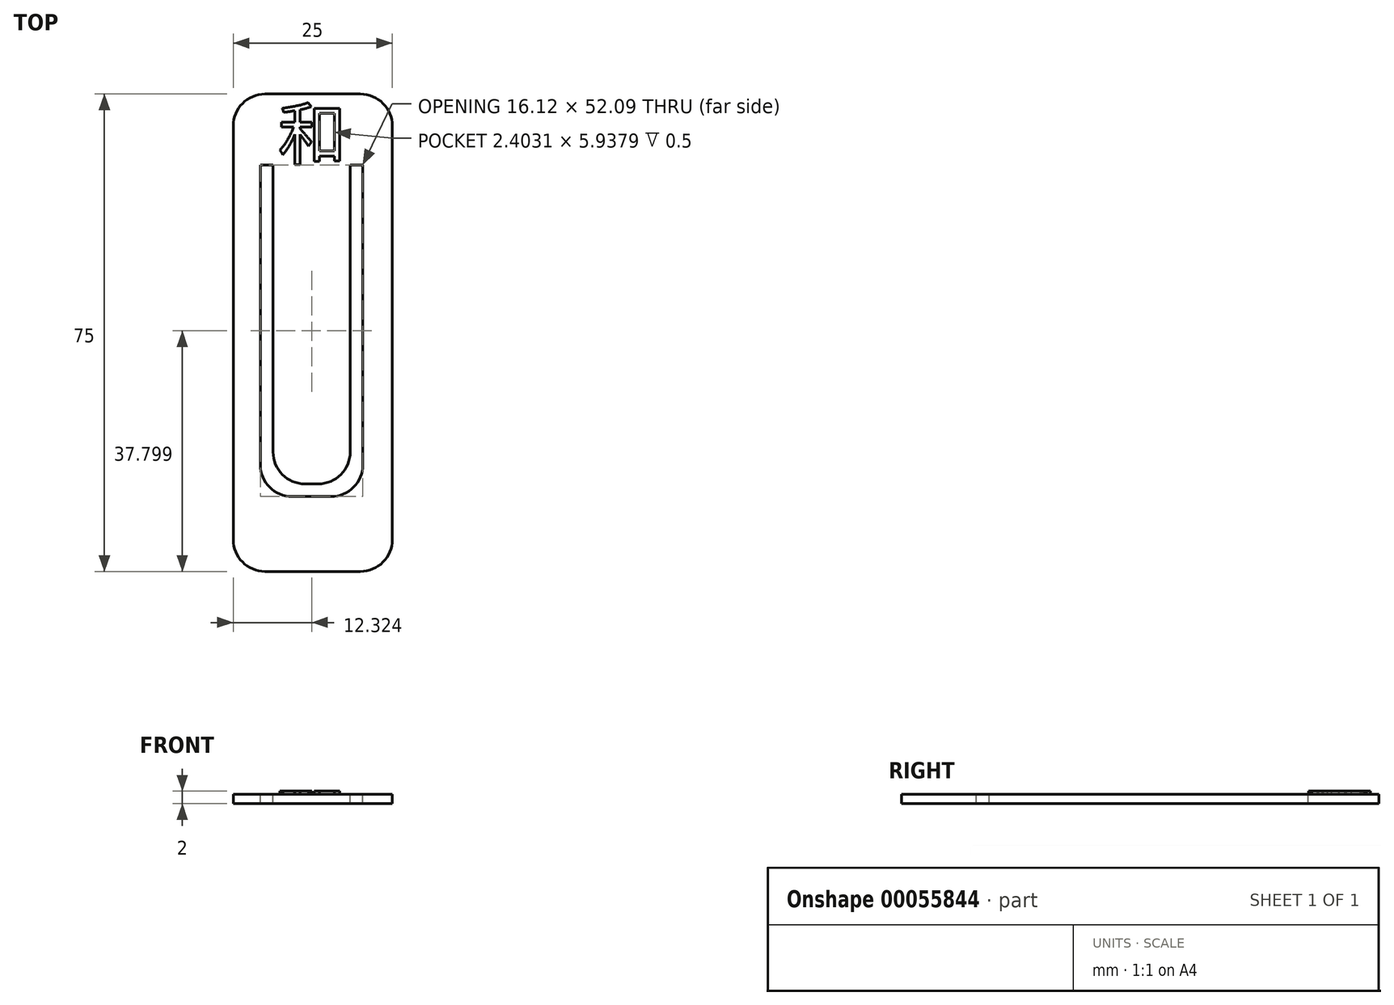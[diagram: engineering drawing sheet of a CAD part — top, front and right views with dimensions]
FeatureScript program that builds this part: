
annotation { "Feature Type Name" : "Feature", "Feature Type Description" : "" }
export const myFeature = defineFeature(function(context is Context, id is Id, definition is map)
    precondition{}
    {
        {
            var Q0;
            Q0=qCreatedBy(makeId("Top.planeOp"),FACE);
            var sketch = newSketch(context, id + "F0", { "sketchPlane" : qUnion([Q0])});
            skLineSegment(sketch, "E0.bottom", {"start": v(-9.97, 72.6) * mm, "end": v(15.03, 72.6) * mm});
            skLineSegment(sketch, "E0.top", {"start": v(-9.97, -2.4) * mm, "end": v(15.03, -2.4) * mm});
            skLineSegment(sketch, "E0.left", {"start": v(-9.97, 72.6) * mm, "end": v(-9.97, -2.4) * mm});
            skLineSegment(sketch, "E0.right", {"start": v(15.03, 72.6) * mm, "end": v(15.03, -2.4) * mm});
            skSolve(sketch);
        }
        {
            var Q0;
            Q0=makeQuery(id+"F0.imprint","IMPRINT",FACE,{"disambiguationData":[TD([[makeQuery(id+"F0.imprint","IMPRINT",EDGE,{"derivedFrom":sQuery(id+"F0.wireOp",EDGE,"E0.bottom")}),-1.0]])]});
            extrude(context, id + "F1", {"entities" : qUnion([Q0]), "depth" : 1.5 * mm});
        }
        {
            var Q0;
            Q0=makeQuery(id+"F1.opExtrude","CAP_FACE",FACE,{"disambiguationData":[OSD([sQuery(id+"F0.wireOp",EDGE,"E0.bottom"),sQuery(id+"F0.wireOp",EDGE,"E0.top"),sQuery(id+"F0.wireOp",EDGE,"E0.left"),sQuery(id+"F0.wireOp",EDGE,"E0.right")])],"isStart":false});
            var sketch = newSketch(context, id + "F2", { "sketchPlane" : qUnion([Q0])});
            skLineSegment(sketch, "E1", {"start": v(-5.7, 61.46) * mm, "end": v(-5.7, 9.36) * mm});
            skLineSegment(sketch, "E2", {"start": v(-5.7, 9.36) * mm, "end": v(10.41, 9.36) * mm});
            skLineSegment(sketch, "E3", {"start": v(10.41, 9.36) * mm, "end": v(10.41, 61.46) * mm});
            skLineSegment(sketch, "E4.0", {"start": v(8.41, 11.36) * mm, "end": v(8.41, 61.46) * mm});
            skLineSegment(sketch, "E4.1", {"start": v(-3.7, 11.36) * mm, "end": v(8.41, 11.36) * mm});
            skLineSegment(sketch, "E4.2", {"start": v(-3.7, 61.46) * mm, "end": v(-3.7, 11.36) * mm});
            skLineSegment(sketch, "E5", {"start": v(-5.7, 61.46) * mm, "end": v(-3.7, 61.46) * mm});
            skLineSegment(sketch, "E6", {"start": v(8.41, 61.46) * mm, "end": v(10.41, 61.46) * mm});
            skSolve(sketch);
        }
        {
            var Q0;
            Q0=makeQuery(id+"F2.imprint","IMPRINT",FACE,{"disambiguationData":[TD([[makeQuery(id+"F2.imprint","IMPRINT",EDGE,{"derivedFrom":sQuery(id+"F2.wireOp",EDGE,"E1")}),1.0]])]});
            extrude(context, id + "F3", {"entities" : qUnion([Q0]), "operationType" : NewBodyOperationType.REMOVE, "oppositeDirection" : true, "depth" : 5 * mm});
        }
        {
            var Q0;
            Q0=makeQuery(id+"F3.boolean.opBoolean","COPY",EDGE,{"derivedFrom":makeQuery(id+"F3.opExtrude","SWEPT_EDGE",EDGE,{"disambiguationData":[OSD([sQuery(id+"F2.wireOp",EDGE,"E4.0"),sQuery(id+"F2.wireOp",EDGE,"E4.1")])]})});
            var Q1;
            Q1=makeQuery(id+"F3.boolean.opBoolean","COPY",EDGE,{"derivedFrom":makeQuery(id+"F3.opExtrude","SWEPT_EDGE",EDGE,{"disambiguationData":[OSD([sQuery(id+"F2.wireOp",EDGE,"E4.1"),sQuery(id+"F2.wireOp",EDGE,"E4.2")])]})});
            var Q2;
            Q2=makeQuery(id+"F3.boolean.opBoolean","COPY",EDGE,{"derivedFrom":makeQuery(id+"F3.opExtrude","SWEPT_EDGE",EDGE,{"disambiguationData":[OSD([sQuery(id+"F2.wireOp",EDGE,"E2"),sQuery(id+"F2.wireOp",EDGE,"E3")])]})});
            var Q3;
            Q3=makeQuery(id+"F3.boolean.opBoolean","COPY",EDGE,{"derivedFrom":makeQuery(id+"F3.opExtrude","SWEPT_EDGE",EDGE,{"disambiguationData":[OSD([sQuery(id+"F2.wireOp",EDGE,"E1"),sQuery(id+"F2.wireOp",EDGE,"E2")])]})});
            var Q4;
            Q4=makeQuery(id+"F1.opExtrude","SWEPT_EDGE",EDGE,{"disambiguationData":[OSD([sQuery(id+"F0.wireOp",EDGE,"E0.top"),sQuery(id+"F0.wireOp",EDGE,"E0.left")])]});
            var Q5;
            Q5=makeQuery(id+"F1.opExtrude","SWEPT_EDGE",EDGE,{"disambiguationData":[OSD([sQuery(id+"F0.wireOp",EDGE,"E0.top"),sQuery(id+"F0.wireOp",EDGE,"E0.right")])]});
            var Q6;
            Q6=makeQuery(id+"F1.opExtrude","SWEPT_EDGE",EDGE,{"disambiguationData":[OSD([sQuery(id+"F0.wireOp",EDGE,"E0.bottom"),sQuery(id+"F0.wireOp",EDGE,"E0.right")])]});
            var Q7;
            Q7=makeQuery(id+"F1.opExtrude","SWEPT_EDGE",EDGE,{"disambiguationData":[OSD([sQuery(id+"F0.wireOp",EDGE,"E0.bottom"),sQuery(id+"F0.wireOp",EDGE,"E0.left")])]});
            fillet(context, id + "F4", {"entities" : qUnion([Q0, Q1, Q2, Q3, Q4, Q5, Q6, Q7]), "radius" : 5 * mm, "tangentPropagation" : true, "allowEdgeOverflow" : false});
        }
        {
            var Q0;
            Q0=makeQuery(id+"F1.opExtrude","CAP_FACE",FACE,{"disambiguationData":[OSD([sQuery(id+"F0.wireOp",EDGE,"E0.bottom"),sQuery(id+"F0.wireOp",EDGE,"E0.top"),sQuery(id+"F0.wireOp",EDGE,"E0.left"),sQuery(id+"F0.wireOp",EDGE,"E0.right")])],"isStart":false});
            var sketch = newSketch(context, id + "F5", { "sketchPlane" : qUnion([Q0])});
            skText(sketch, "E7", { "text": "和", "fontName": "NotoSansCJKtc-Regular.otf"});
            const initialGuessF5  = {"E7": [-0.00294, 0.06235, 1, 0, 0.00776]};
            skSetInitialGuess(sketch, initialGuessF5);
            skSolve(sketch);
        }
        {
            var Q0;
            Q0=makeQuery(id+"F5.imprint","IMPRINT",FACE,{"disambiguationData":[TD([[makeQuery(id+"F5.imprint","IMPRINT",EDGE,{"derivedFrom":sQuery(id+"F5.wireOp",EDGE,"E7.sketch_text.stroke-0")}),1.0]])]});
            var Q1;
            Q1=makeQuery(id+"F5.imprint","IMPRINT",FACE,{"disambiguationData":[TD([[makeQuery(id+"F5.imprint","IMPRINT",EDGE,{"derivedFrom":sQuery(id+"F5.wireOp",EDGE,"E7.sketch_text.stroke-23")}),1.0]])]});
            extrude(context, id + "F6", {"entities" : qUnion([Q0, Q1]), "operationType" : NewBodyOperationType.ADD, "depth" : 0.5 * mm});
        }
    });
